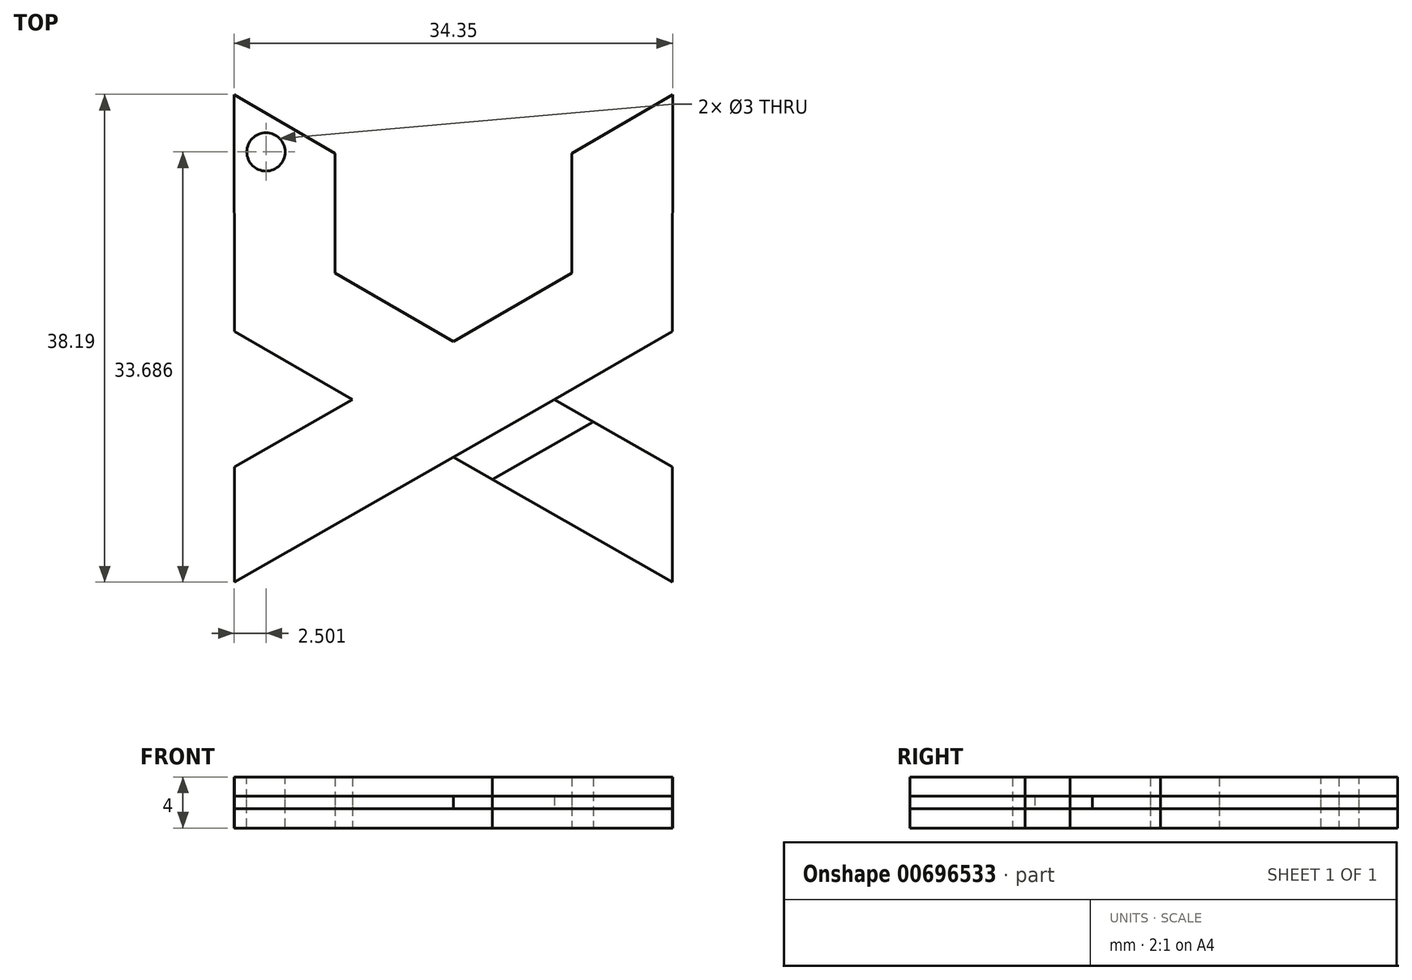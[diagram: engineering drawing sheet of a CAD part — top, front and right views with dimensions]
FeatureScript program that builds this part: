
annotation { "Feature Type Name" : "Feature", "Feature Type Description" : "" }
export const myFeature = defineFeature(function(context is Context, id is Id, definition is map)
    precondition{}
    {
        {
            var Q0;
            Q0=qCreatedBy(makeId("Top.planeOp"),FACE);
            var sketch = newSketch(context, id + "F0", { "sketchPlane" : qUnion([Q0])});
            skLineSegment(sketch, "E0", {"start": v(-37.15, 39.96) * mm, "end": v(-29.25, 35.35) * mm});
            skLineSegment(sketch, "E1", {"start": v(-29.25, 35.35) * mm, "end": v(-29.25, 25.99) * mm});
            skLineSegment(sketch, "E2", {"start": v(-29.25, 25.99) * mm, "end": v(-19.98, 20.6) * mm});
            skLineSegment(sketch, "E3", {"start": v(-19.98, 20.6) * mm, "end": v(-19.98, 11.56) * mm});
            skLineSegment(sketch, "E4", {"start": v(-19.98, 11.56) * mm, "end": v(-37.13, 1.77) * mm});
            skLineSegment(sketch, "E5", {"start": v(-37.13, 1.77) * mm, "end": v(-37.13, 10.8) * mm});
            skLineSegment(sketch, "E6", {"start": v(-37.13, 10.8) * mm, "end": v(-27.88, 16.07) * mm});
            skLineSegment(sketch, "E7", {"start": v(-27.88, 16.07) * mm, "end": v(-37.13, 21.4) * mm});
            skLineSegment(sketch, "E8", {"start": v(-37.13, 21.4) * mm, "end": v(-37.15, 39.96) * mm});
            skLineSegment(sketch, "E9.MirrorCS", {"start": v(-10.7, 25.99) * mm, "end": v(-19.98, 20.6) * mm});
            skLineSegment(sketch, "E10.MirrorCS", {"start": v(-10.7, 35.35) * mm, "end": v(-10.7, 25.99) * mm});
            skLineSegment(sketch, "E11.MirrorCS", {"start": v(-2.8, 39.96) * mm, "end": v(-10.7, 35.35) * mm});
            skLineSegment(sketch, "E12.MirrorCS", {"start": v(-2.83, 21.4) * mm, "end": v(-2.8, 39.96) * mm});
            skLineSegment(sketch, "E13.MirrorCS", {"start": v(-12.08, 16.07) * mm, "end": v(-2.83, 21.4) * mm});
            skLineSegment(sketch, "E14.MirrorCS", {"start": v(-2.83, 10.8) * mm, "end": v(-12.08, 16.07) * mm});
            skLineSegment(sketch, "E15.MirrorCS", {"start": v(-2.83, 1.77) * mm, "end": v(-2.83, 10.8) * mm});
            skLineSegment(sketch, "E16.MirrorCS", {"start": v(-19.98, 11.56) * mm, "end": v(-2.83, 1.77) * mm});
            skLineSegment(sketch, "E17", {"start": v(-19.98, 11.56) * mm, "end": v(-12.08, 16.07) * mm});
            skLineSegment(sketch, "E18", {"start": v(-16.92, 9.81) * mm, "end": v(-9, 14.32) * mm});
            skSolve(sketch);
        }
        {
            var Q0;
            Q0=makeQuery(id+"F0.imprint","IMPRINT",FACE,{"disambiguationData":[TD([[makeQuery(id+"F0.imprint","IMPRINT",EDGE,{"derivedFrom":sQuery(id+"F0.wireOp",EDGE,"E3")}),1.0]])]});
            var Q1;
            Q1=makeQuery(id+"F0.imprint","IMPRINT",FACE,{"disambiguationData":[TD([[makeQuery(id+"F0.imprint","IMPRINT",EDGE,{"derivedFrom":sQuery(id+"F0.wireOp",EDGE,"E0")}),-1.0]])]});
            var Q2;
            {var subQ0=sQuery(id+"F0.wireOp",EDGE,"E17");Q2=makeQuery(id+"F0.imprint","IMPRINT",FACE,{"disambiguationData":[TD([[makeQuery(id+"F0.imprint","IMPRINT",EDGE,{"derivedFrom":subQ0}),-1.0]])]});}
            var Q3;
            {var subQ0=sQuery(id+"F0.wireOp",EDGE,"E15.MirrorCS");Q3=makeQuery(id+"F0.imprint","IMPRINT",FACE,{"disambiguationData":[TD([[makeQuery(id+"F0.imprint","IMPRINT",EDGE,{"derivedFrom":subQ0}),1.0]])]});}
            extrude(context, id + "F1", {"entities" : qUnion([Q0, Q1, Q2, Q3]), "depth" : 1 * mm, "offsetDistance" : 25.4 * mm, "symmetric" : true});
        }
        {
            var Q0;
            {var subQ0=sQuery(id+"F0.wireOp",EDGE,"E15.MirrorCS");Q0=makeQuery(id+"F0.imprint","IMPRINT",FACE,{"disambiguationData":[TD([[makeQuery(id+"F0.imprint","IMPRINT",EDGE,{"derivedFrom":subQ0}),1.0]])]});}
            var Q1;
            Q1=makeQuery(id+"F0.imprint","IMPRINT",FACE,{"disambiguationData":[TD([[makeQuery(id+"F0.imprint","IMPRINT",EDGE,{"derivedFrom":sQuery(id+"F0.wireOp",EDGE,"E3")}),1.0]])]});
            var Q2;
            Q2=makeQuery(id+"F0.imprint","IMPRINT",FACE,{"disambiguationData":[TD([[makeQuery(id+"F0.imprint","IMPRINT",EDGE,{"derivedFrom":sQuery(id+"F0.wireOp",EDGE,"E0")}),-1.0]])]});
            extrude(context, id + "F2", {"entities" : qUnion([Q0, Q1, Q2]), "depth" : 4 * mm, "offsetDistance" : 25 * mm, "symmetric" : true});
        }
        {
            var Q0;
            Q0=makeQuery(id+"F2.opExtrude","CAP_FACE",FACE,{"disambiguationData":[OSD([sQuery(id+"F0.wireOp",EDGE,"E0"),sQuery(id+"F0.wireOp",EDGE,"E1"),sQuery(id+"F0.wireOp",EDGE,"E2"),sQuery(id+"F0.wireOp",EDGE,"E4"),sQuery(id+"F0.wireOp",EDGE,"E5"),sQuery(id+"F0.wireOp",EDGE,"E6"),sQuery(id+"F0.wireOp",EDGE,"E7"),sQuery(id+"F0.wireOp",EDGE,"E8"),sQuery(id+"F0.wireOp",EDGE,"E9.MirrorCS"),sQuery(id+"F0.wireOp",EDGE,"E10.MirrorCS"),sQuery(id+"F0.wireOp",EDGE,"E11.MirrorCS"),sQuery(id+"F0.wireOp",EDGE,"E12.MirrorCS"),sQuery(id+"F0.wireOp",EDGE,"E13.MirrorCS"),sQuery(id+"F0.wireOp",EDGE,"E17")])],"isStart":false});
            var sketch = newSketch(context, id + "F3", { "sketchPlane" : qUnion([Q0])});
            skCircle(sketch, "E19", {"center": v(-34.65, 35.46) * mm, "radius": 1.5 * mm});
            skSolve(sketch);
        }
        {
            var Q0;
            Q0=makeQuery(id+"F3.imprint","IMPRINT",FACE,{"disambiguationData":[TD([[makeQuery(id+"F3.imprint","IMPRINT",EDGE,{"derivedFrom":sQuery(id+"F3.wireOp",EDGE,"E19")}),1.0]])]});
            extrude(context, id + "F4", {"entities" : qUnion([Q0]), "operationType" : NewBodyOperationType.REMOVE, "oppositeDirection" : true, "depth" : 25 * mm, "offsetDistance" : 25 * mm, "symmetric" : true});
        }
    });
